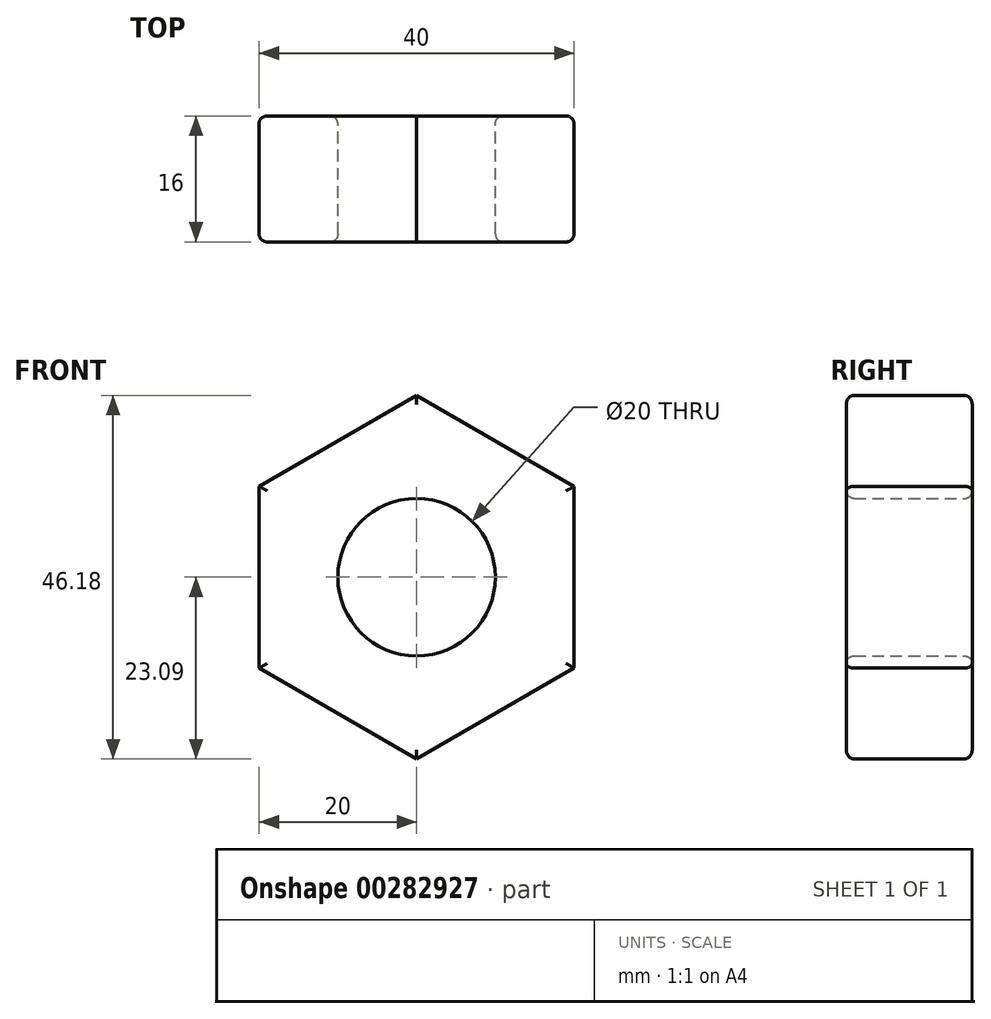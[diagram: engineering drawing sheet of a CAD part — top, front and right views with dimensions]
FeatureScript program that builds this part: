
annotation { "Feature Type Name" : "Feature", "Feature Type Description" : "" }
export const myFeature = defineFeature(function(context is Context, id is Id, definition is map)
    precondition{}
    {
        {
            var Q0;
            Q0=qCreatedBy(makeId("Front.planeOp"),FACE);
            var sketch = newSketch(context, id + "F0", { "sketchPlane" : qUnion([Q0])});
            skCircle(sketch, "E0.cCircle", {"center": v(0, 0) * mm, "radius": 23.1 * mm, "construction": true});
            skLineSegment(sketch, "E0.0", {"start": v(0, -23.1) * mm, "end": v(-20, -11.55) * mm});
            skLineSegment(sketch, "E0.1", {"start": v(-20, -11.55) * mm, "end": v(-20, 11.55) * mm});
            skLineSegment(sketch, "E0.2", {"start": v(-20, 11.55) * mm, "end": v(0, 23.1) * mm});
            skLineSegment(sketch, "E0.3", {"start": v(0, 23.1) * mm, "end": v(20, 11.55) * mm});
            skLineSegment(sketch, "E0.4", {"start": v(20, 11.55) * mm, "end": v(20, -11.55) * mm});
            skLineSegment(sketch, "E0.5", {"start": v(20, -11.55) * mm, "end": v(0, -23.1) * mm});
            skCircle(sketch, "E1", {"center": v(0, 0) * mm, "radius": 10 * mm});
            skSolve(sketch);
        }
        {
            var Q0;
            Q0 = qSketchRegion(id + "F0", true);
            extrude(context, id + "F1", {"entities" : qUnion([Q0]), "depth" : 16 * mm});
        }
        {
            var Q0;
            Q0=makeQuery(id+"F1.opExtrude","CAP_FACE",FACE,{"disambiguationData":[OSD([sQuery(id+"F0.wireOp",EDGE,"E0.0"),sQuery(id+"F0.wireOp",EDGE,"E0.1"),sQuery(id+"F0.wireOp",EDGE,"E0.2"),sQuery(id+"F0.wireOp",EDGE,"E0.3"),sQuery(id+"F0.wireOp",EDGE,"E0.4"),sQuery(id+"F0.wireOp",EDGE,"E0.5"),sQuery(id+"F0.wireOp",EDGE,"E1")])],"isStart":false});
            fillet(context, id + "F2", {"entities" : qUnion([Q0]), "radius" : 1 * mm, "tangentPropagation" : true, "allowEdgeOverflow" : false});
        }
        {
            var Q0;
            Q0=makeQuery(id+"F1.opExtrude","CAP_FACE",FACE,{"disambiguationData":[OSD([sQuery(id+"F0.wireOp",EDGE,"E0.0"),sQuery(id+"F0.wireOp",EDGE,"E0.1"),sQuery(id+"F0.wireOp",EDGE,"E0.2"),sQuery(id+"F0.wireOp",EDGE,"E0.3"),sQuery(id+"F0.wireOp",EDGE,"E0.4"),sQuery(id+"F0.wireOp",EDGE,"E0.5"),sQuery(id+"F0.wireOp",EDGE,"E1")])],"isStart":true});
            fillet(context, id + "F3", {"entities" : qUnion([Q0]), "radius" : 1 * mm, "tangentPropagation" : true, "allowEdgeOverflow" : false});
        }
    });
